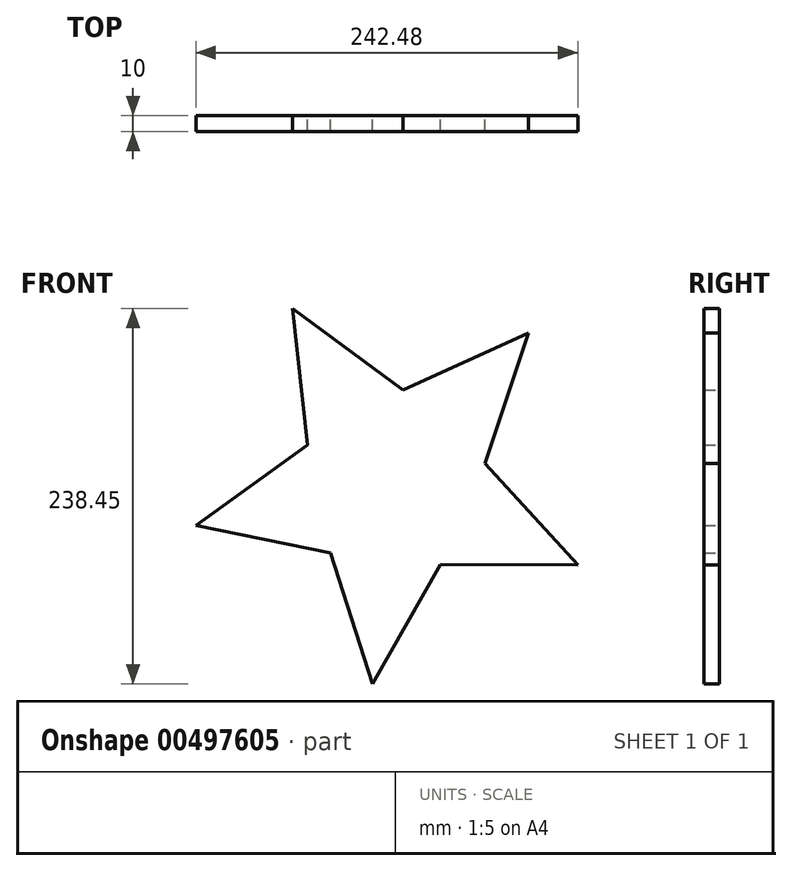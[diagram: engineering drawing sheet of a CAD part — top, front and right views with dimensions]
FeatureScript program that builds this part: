
annotation { "Feature Type Name" : "Feature", "Feature Type Description" : "" }
export const myFeature = defineFeature(function(context is Context, id is Id, definition is map)
    precondition{}
    {
        {
            var Q0;
            Q0=qCreatedBy(makeId("Front.planeOp"),FACE);
            var sketch = newSketch(context, id + "F0", { "sketchPlane" : qUnion([Q0])});
            skPoint(sketch, "E0.0.midPoint", {"position": v(-24.1, 41.7) * mm});
            skLineSegment(sketch, "E1", {"start": v(-64.15, 110.97) * mm, "end": v(-54.41, 24.19) * mm});
            skLineSegment(sketch, "E2", {"start": v(-64.15, 110.97) * mm, "end": v(6.2, 59.22) * mm});
            skLineSegment(sketch, "E3", {"start": v(6.2, 59.22) * mm, "end": v(85.71, 95.3) * mm});
            skLineSegment(sketch, "E4", {"start": v(58.24, 12.41) * mm, "end": v(85.71, 95.3) * mm});
            skLineSegment(sketch, "E5", {"start": v(58.24, 12.41) * mm, "end": v(117.12, -52.07) * mm});
            skLineSegment(sketch, "E6", {"start": v(29.8, -51.55) * mm, "end": v(117.12, -52.07) * mm});
            skLineSegment(sketch, "E7", {"start": v(29.8, -51.55) * mm, "end": v(-13.33, -127.48) * mm});
            skLineSegment(sketch, "E8", {"start": v(-13.33, -127.48) * mm, "end": v(-39.82, -44.27) * mm});
            skLineSegment(sketch, "E9", {"start": v(-39.82, -44.27) * mm, "end": v(-125.36, -26.72) * mm});
            skLineSegment(sketch, "E10", {"start": v(-125.36, -26.72) * mm, "end": v(-54.41, 24.19) * mm});
            skSolve(sketch);
        }
        {
            var Q0;
            Q0 = qSketchRegion(id + "F0", true);
            extrude(context, id + "F1", {"entities" : qUnion([Q0]), "depth" : 10 * mm});
        }
    });
